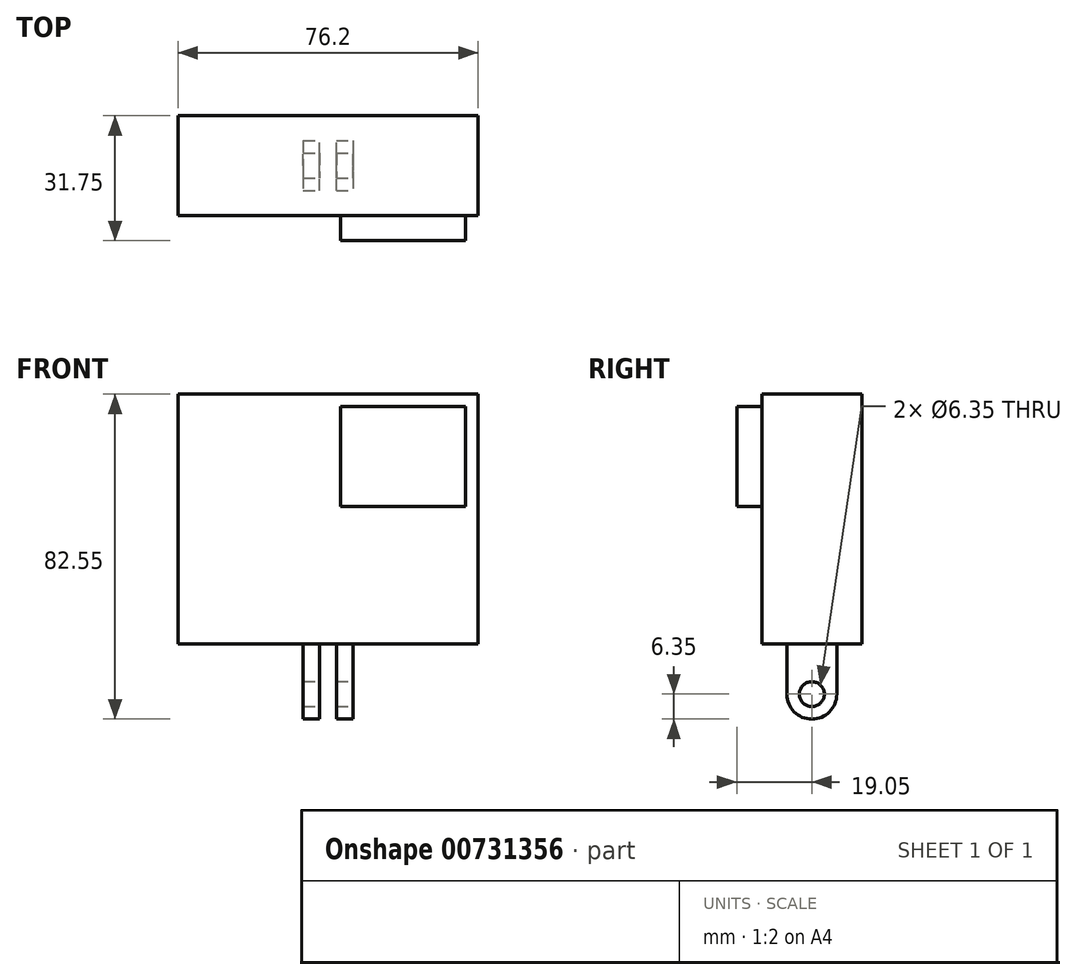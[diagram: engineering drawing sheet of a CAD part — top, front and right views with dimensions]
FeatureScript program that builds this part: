
annotation { "Feature Type Name" : "Feature", "Feature Type Description" : "" }
export const myFeature = defineFeature(function(context is Context, id is Id, definition is map)
    precondition{}
    {
        {
            var Q0;
            Q0=qCreatedBy(makeId("Front.planeOp"),FACE);
            var sketch = newSketch(context, id + "F0", { "sketchPlane" : qUnion([Q0])});
            skLineSegment(sketch, "E0.bottom", {"start": v(38.1, 31.75) * mm, "end": v(-38.1, 31.75) * mm});
            skLineSegment(sketch, "E0.top", {"start": v(38.1, -31.75) * mm, "end": v(-38.1, -31.75) * mm});
            skLineSegment(sketch, "E0.left", {"start": v(38.1, 31.75) * mm, "end": v(38.1, -31.75) * mm});
            skLineSegment(sketch, "E0.right", {"start": v(-38.1, 31.75) * mm, "end": v(-38.1, -31.75) * mm});
            skPoint(sketch, "E0.middle", {"position": v(0, 0) * mm});
            skLineSegment(sketch, "E1.bottom", {"start": v(34.92, 28.58) * mm, "end": v(3.17, 28.58) * mm});
            skLineSegment(sketch, "E1.top", {"start": v(34.92, 3.18) * mm, "end": v(3.17, 3.18) * mm});
            skLineSegment(sketch, "E1.left", {"start": v(34.92, 28.58) * mm, "end": v(34.92, 3.18) * mm});
            skLineSegment(sketch, "E1.right", {"start": v(3.17, 28.58) * mm, "end": v(3.17, 3.18) * mm});
            skPoint(sketch, "E1.middle", {"position": v(19.05, 15.88) * mm});
            skSolve(sketch);
        }
        {
            var Q0;
            Q0=makeQuery(id+"F0.imprint","IMPRINT",FACE,{"disambiguationData":[TD([[makeQuery(id+"F0.imprint","IMPRINT",EDGE,{"derivedFrom":sQuery(id+"F0.wireOp",EDGE,"E0.bottom")}),1.0]])]});
            extrude(context, id + "F1", {"entities" : qUnion([Q0]), "depth" : 25.4 * mm, "offsetDistance" : 25.4 * mm});
        }
        {
            var Q0;
            Q0=makeQuery(id+"F1.opExtrude","CAP_FACE",FACE,{"disambiguationData":[OSD([sQuery(id+"F0.wireOp",EDGE,"E0.bottom"),sQuery(id+"F0.wireOp",EDGE,"E0.top"),sQuery(id+"F0.wireOp",EDGE,"E0.left"),sQuery(id+"F0.wireOp",EDGE,"E0.right"),sQuery(id+"F0.wireOp",EDGE,"E1.bottom"),sQuery(id+"F0.wireOp",EDGE,"E1.top"),sQuery(id+"F0.wireOp",EDGE,"E1.left"),sQuery(id+"F0.wireOp",EDGE,"E1.right")])],"isStart":true});
            var sketch = newSketch(context, id + "F2", { "sketchPlane" : qUnion([Q0])});
            skLineSegment(sketch, "E2.bottom", {"start": v(-34.92, 28.58) * mm, "end": v(-3.17, 28.58) * mm});
            skLineSegment(sketch, "E2.top", {"start": v(-34.92, 3.18) * mm, "end": v(-3.17, 3.18) * mm});
            skLineSegment(sketch, "E2.left", {"start": v(-34.92, 28.58) * mm, "end": v(-34.92, 3.18) * mm});
            skLineSegment(sketch, "E2.right", {"start": v(-3.17, 28.58) * mm, "end": v(-3.17, 3.18) * mm});
            skSolve(sketch);
        }
        {
            var Q0;
            Q0 = qSketchRegion(id + "F2", true);
            extrude(context, id + "F3", {"entities" : qUnion([Q0]), "operationType" : NewBodyOperationType.ADD, "oppositeDirection" : true, "depth" : 31.75 * mm, "offsetDistance" : 25.4 * mm});
        }
        {
            var Q0;
            Q0=makeQuery(id+"F1.opExtrude","SWEPT_FACE",FACE,{"disambiguationData":[OSD([sQuery(id+"F0.wireOp",EDGE,"E0.right")])]});
            cPlane(context, id + "F4", {"entities" : qUnion([Q0]), "cplaneType" : CPlaneType.OFFSET, "offset" : 38.1 * mm, "oppositeDirection" : true, "width" : 152.4 * mm, "height" : 152.4 * mm});
        }
        {
            var Q0;
            Q0=qCreatedBy(id+"F4.planeOp",FACE);
            var sketch = newSketch(context, id + "F5", { "sketchPlane" : qUnion([Q0])});
            skLineSegment(sketch, "E3", {"start": v(6.35, -44.45) * mm, "end": v(6.35, -31.75) * mm});
            skLineSegment(sketch, "E4", {"start": v(6.35, -31.75) * mm, "end": v(19.05, -31.75) * mm});
            skLineSegment(sketch, "E5", {"start": v(19.05, -31.75) * mm, "end": v(19.05, -44.45) * mm});
            skArc(sketch, "E6", {"start": v(6.35, -44.45) * mm, "mid": v(12.7, -50.8) * mm, "end": v(19.05, -44.45) * mm});
            skSolve(sketch);
        }
        {
            var Q0;
            Q0 = qSketchRegion(id + "F5", true);
            extrude(context, id + "F6", {"entities" : qUnion([Q0]), "operationType" : NewBodyOperationType.ADD, "endBound" : BoundingType.SYMMETRIC, "depth" : 12.7 * mm, "offsetDistance" : 25.4 * mm});
        }
        {
            var Q0;
            Q0=qCreatedBy(makeId("Front.planeOp"),FACE);
            var sketch = newSketch(context, id + "F7", { "sketchPlane" : qUnion([Q0])});
            skLineSegment(sketch, "E7.bottom", {"start": v(-2.12, -31.75) * mm, "end": v(2.12, -31.75) * mm});
            skLineSegment(sketch, "E7.top", {"start": v(-2.12, -50.8) * mm, "end": v(2.12, -50.8) * mm});
            skLineSegment(sketch, "E7.left", {"start": v(-2.12, -31.75) * mm, "end": v(-2.12, -50.8) * mm});
            skLineSegment(sketch, "E7.right", {"start": v(2.12, -31.75) * mm, "end": v(2.12, -50.8) * mm});
            skPoint(sketch, "E7.middle", {"position": v(0, -41.28) * mm});
            skSolve(sketch);
        }
        {
            var Q0;
            Q0 = qSketchRegion(id + "F7", true);
            extrude(context, id + "F8", {"entities" : qUnion([Q0]), "operationType" : NewBodyOperationType.REMOVE, "endBound" : BoundingType.THROUGH_ALL, "depth" : 25.4 * mm, "offsetDistance" : 25.4 * mm});
        }
        {
            var Q0;
            Q0=makeQuery(id+"F6.opExtrude","CAP_FACE",FACE,{"disambiguationData":[OSD([sQuery(id+"F5.wireOp",EDGE,"E3"),sQuery(id+"F5.wireOp",EDGE,"E4"),sQuery(id+"F5.wireOp",EDGE,"E5"),sQuery(id+"F5.wireOp",EDGE,"E6")])],"isStart":true});
            var sketch = newSketch(context, id + "F9", { "sketchPlane" : qUnion([Q0])});
            skCircle(sketch, "E8", {"center": v(-12.7, -44.45) * mm, "radius": 3.18 * mm});
            skSolve(sketch);
        }
        {
            var Q0;
            Q0 = qSketchRegion(id + "F9", true);
            extrude(context, id + "F10", {"entities" : qUnion([Q0]), "operationType" : NewBodyOperationType.REMOVE, "endBound" : BoundingType.THROUGH_ALL, "oppositeDirection" : true, "depth" : 25.4 * mm, "offsetDistance" : 25.4 * mm});
        }
    });
